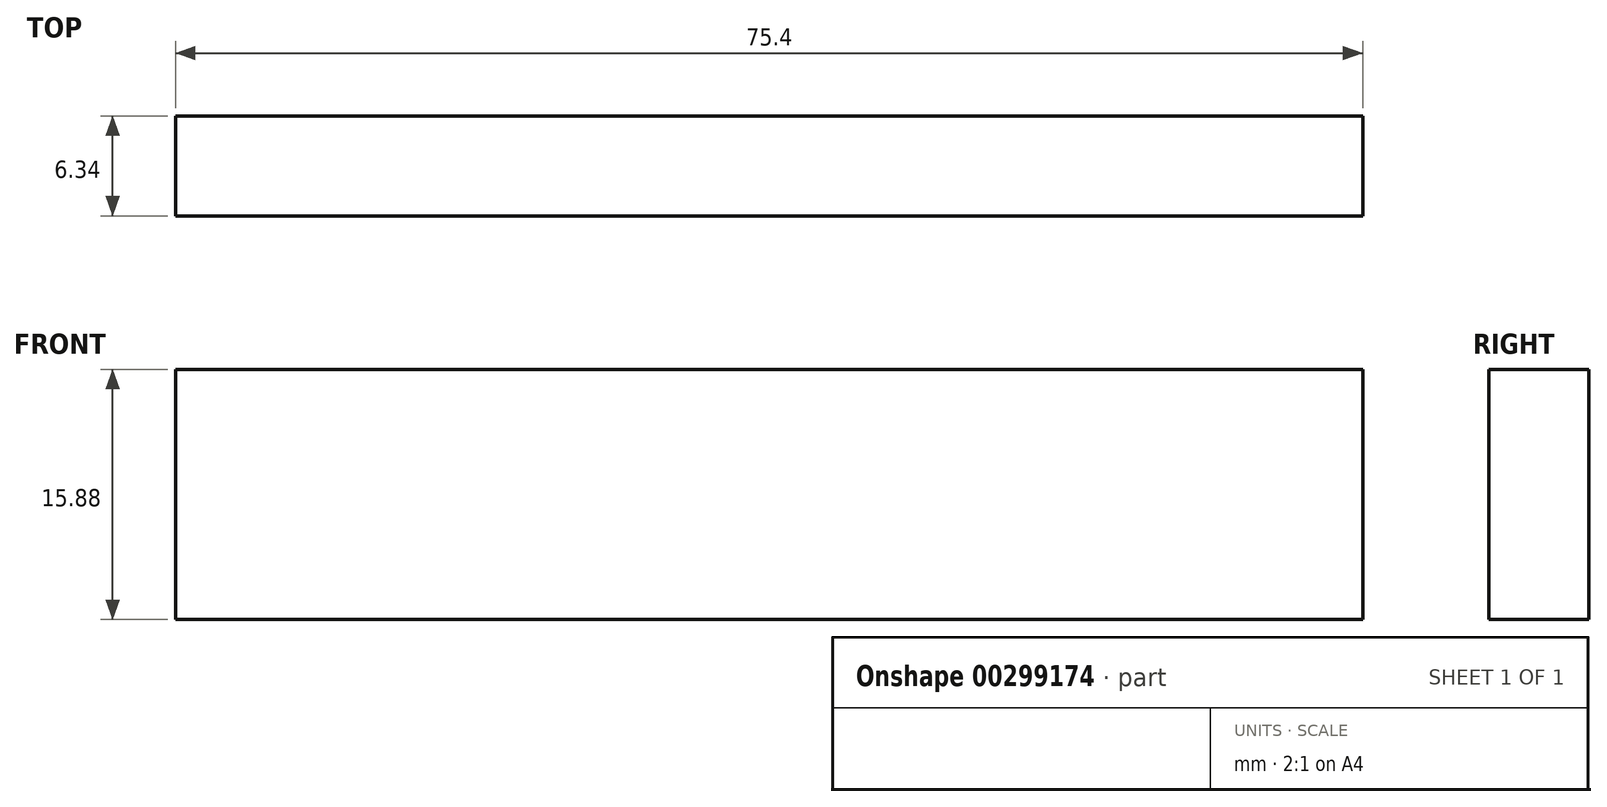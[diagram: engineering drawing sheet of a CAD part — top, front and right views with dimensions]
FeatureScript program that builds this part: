
annotation { "Feature Type Name" : "Feature", "Feature Type Description" : "" }
export const myFeature = defineFeature(function(context is Context, id is Id, definition is map)
    precondition{}
    {
        {
            var Q0;
            Q0=qCreatedBy(makeId("Front.planeOp"),FACE);
            var sketch = newSketch(context, id + "F0", { "sketchPlane" : qUnion([Q0])});
            skLineSegment(sketch, "E0.bottom", {"start": v(37.7, 7.94) * mm, "end": v(-37.7, 7.94) * mm});
            skLineSegment(sketch, "E0.top", {"start": v(37.7, -7.94) * mm, "end": v(-37.7, -7.94) * mm});
            skLineSegment(sketch, "E0.left", {"start": v(37.7, 7.94) * mm, "end": v(37.7, -7.94) * mm});
            skLineSegment(sketch, "E0.right", {"start": v(-37.7, 7.94) * mm, "end": v(-37.7, -7.94) * mm});
            skPoint(sketch, "E0.middle", {"position": v(0, 0) * mm});
            skSolve(sketch);
        }
        {
            var Q0;
            Q0 = qSketchRegion(id + "F0", true);
            extrude(context, id + "F1", {"entities" : qUnion([Q0]), "endBound" : BoundingType.SYMMETRIC, "depth" : 6.35 * mm});
        }
    });
